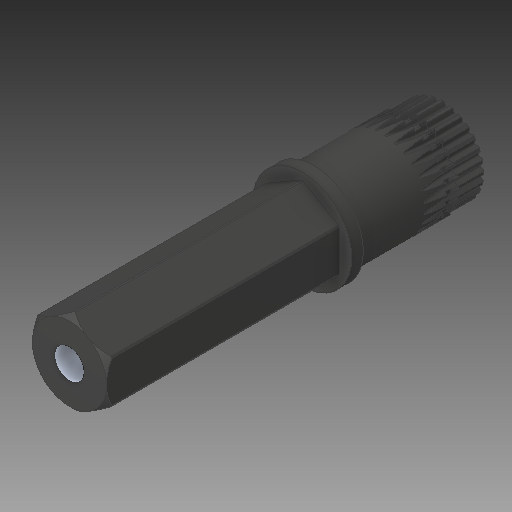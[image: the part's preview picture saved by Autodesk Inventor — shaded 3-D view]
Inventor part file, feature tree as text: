
AUTODESK INVENTOR PART (.ipt)
format: ipt  version: 2018 (Build 220112000, 112)  size: 1,428,480 bytes
history: native  units: in
note: dims shown in document units (in); Inventor stores cm internally (conversion verified against a paired STEP export)
features: fillet x1
ambient origin geometry x8: Origin, YZ Plane, XZ Plane, XY Plane, X Axis, Y Axis, Z Axis, Center Point
bodies: Solid1 (feature_tree)
feature tree (1):
  fillet  "Fillet5"  [1 undecoded]
note: 1 required parameter value undecoded (feature->parameter linkage not recoverable at this tier; creation-order binding heuristic only, values carry confidence <= 0.55)
